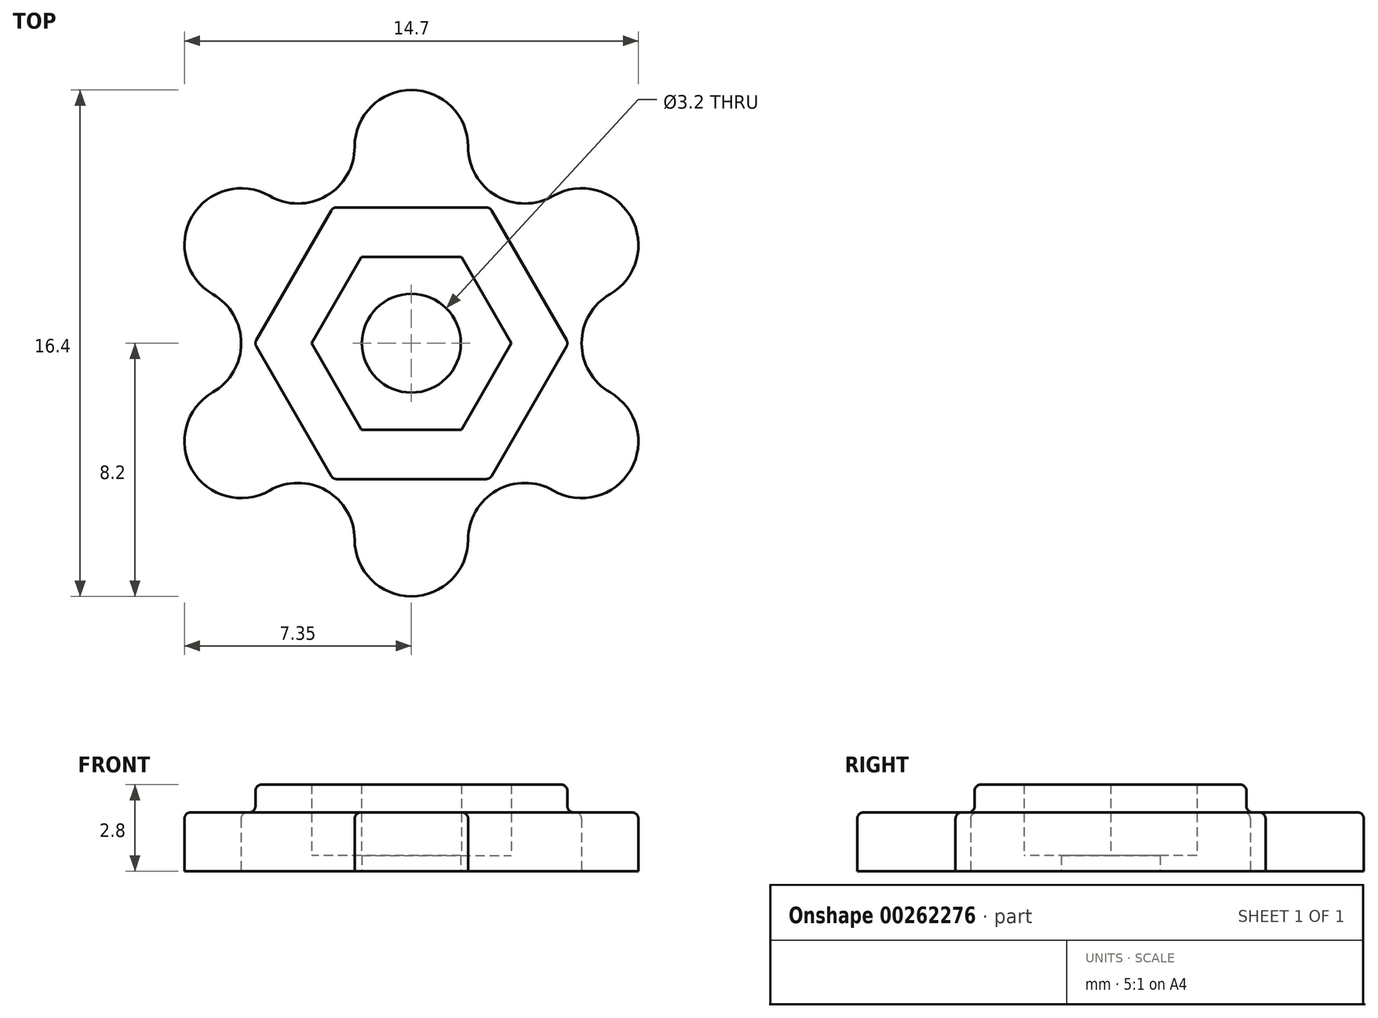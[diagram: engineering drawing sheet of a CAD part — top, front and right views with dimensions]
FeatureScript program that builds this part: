
annotation { "Feature Type Name" : "Feature", "Feature Type Description" : "" }
export const myFeature = defineFeature(function(context is Context, id is Id, definition is map)
    precondition{}
    {
        {
            var Q0;
            Q0=qCreatedBy(makeId("Top.planeOp"),FACE);
            var sketch = newSketch(context, id + "F0", { "sketchPlane" : qUnion([Q0])});
            skCircle(sketch, "E0", {"center": v(0, 0) * mm, "radius": 6.62 * mm, "construction": true});
            skArc(sketch, "E1", {"start": v(1.84, 6.36) * mm, "mid": v(0, 8.2) * mm, "end": v(-1.84, 6.36) * mm});
            skLineSegment(sketch, "E2", {"start": v(1.84, 6.36) * mm, "end": v(-1.84, 6.36) * mm, "construction": true});
            skArc(sketch, "E3", {"start": v(1.84, 6.36) * mm, "mid": v(2.76, 4.77) * mm, "end": v(4.6, 4.77) * mm});
            skLineSegment(sketch, "E4", {"start": v(1.84, 6.36) * mm, "end": v(4.6, 4.77) * mm, "construction": true});
            skArc(sketch, "E5.1.0", {"start": v(-4.6, 4.77) * mm, "mid": v(-7.1, 4.1) * mm, "end": v(-6.43, 1.6) * mm});
            skArc(sketch, "E5.1.1", {"start": v(-4.6, 4.77) * mm, "mid": v(-2.76, 4.77) * mm, "end": v(-1.84, 6.36) * mm});
            skArc(sketch, "E5.2.0", {"start": v(-6.43, -1.6) * mm, "mid": v(-7.1, -4.1) * mm, "end": v(-4.6, -4.77) * mm});
            skArc(sketch, "E5.2.1", {"start": v(-6.43, -1.6) * mm, "mid": v(-5.51, 0) * mm, "end": v(-6.43, 1.6) * mm});
            skArc(sketch, "E5.3.0", {"start": v(-1.84, -6.36) * mm, "mid": v(0, -8.2) * mm, "end": v(1.84, -6.36) * mm});
            skArc(sketch, "E5.3.1", {"start": v(-1.84, -6.36) * mm, "mid": v(-2.76, -4.77) * mm, "end": v(-4.6, -4.77) * mm});
            skArc(sketch, "E5.4.0", {"start": v(4.6, -4.77) * mm, "mid": v(7.1, -4.1) * mm, "end": v(6.43, -1.6) * mm});
            skArc(sketch, "E5.4.1", {"start": v(4.6, -4.77) * mm, "mid": v(2.76, -4.77) * mm, "end": v(1.84, -6.36) * mm});
            skArc(sketch, "E5.5.0", {"start": v(6.43, 1.6) * mm, "mid": v(7.1, 4.1) * mm, "end": v(4.6, 4.77) * mm});
            skArc(sketch, "E5.5.1", {"start": v(6.43, 1.6) * mm, "mid": v(5.51, 0) * mm, "end": v(6.43, -1.6) * mm});
            skCircle(sketch, "E6.cCircle", {"center": v(0, 0) * mm, "radius": 4.4 * mm, "construction": true});
            skLineSegment(sketch, "E6.0", {"start": v(2.54, 4.4) * mm, "end": v(5.08, 0) * mm});
            skLineSegment(sketch, "E6.1", {"start": v(5.08, 0) * mm, "end": v(2.54, -4.4) * mm});
            skLineSegment(sketch, "E6.2", {"start": v(2.54, -4.4) * mm, "end": v(-2.54, -4.4) * mm});
            skLineSegment(sketch, "E6.3", {"start": v(-2.54, -4.4) * mm, "end": v(-5.08, 0) * mm});
            skLineSegment(sketch, "E6.4", {"start": v(-5.08, 0) * mm, "end": v(-2.54, 4.4) * mm});
            skLineSegment(sketch, "E6.5", {"start": v(-2.54, 4.4) * mm, "end": v(2.54, 4.4) * mm});
            skPoint(sketch, "E6.0.midPoint", {"position": v(3.81, 2.2) * mm});
            skCircle(sketch, "E7.cCircle", {"center": v(0, 0) * mm, "radius": 2.8 * mm, "construction": true});
            skLineSegment(sketch, "E7.0", {"start": v(1.62, 2.8) * mm, "end": v(3.23, 0) * mm});
            skLineSegment(sketch, "E7.1", {"start": v(3.23, 0) * mm, "end": v(1.62, -2.8) * mm});
            skLineSegment(sketch, "E7.2", {"start": v(1.62, -2.8) * mm, "end": v(-1.62, -2.8) * mm});
            skLineSegment(sketch, "E7.3", {"start": v(-1.62, -2.8) * mm, "end": v(-3.23, 0) * mm});
            skLineSegment(sketch, "E7.4", {"start": v(-3.23, 0) * mm, "end": v(-1.62, 2.8) * mm});
            skLineSegment(sketch, "E7.5", {"start": v(-1.62, 2.8) * mm, "end": v(1.62, 2.8) * mm});
            skPoint(sketch, "E7.0.midPoint", {"position": v(2.42, 1.4) * mm});
            skCircle(sketch, "E8", {"center": v(0, 0) * mm, "radius": 1.6 * mm});
            skSolve(sketch);
        }
        {
            var Q0;
            Q0=makeQuery(id+"F0.imprint","IMPRINT",FACE,{"disambiguationData":[TD([[makeQuery(id+"F0.imprint","IMPRINT",EDGE,{"derivedFrom":sQuery(id+"F0.wireOp",EDGE,"E1")}),1.0]])]});
            extrude(context, id + "F1", {"entities" : qUnion([Q0]), "depth" : 1.9 * mm});
        }
        {
            var Q0;
            Q0=makeQuery(id+"F0.imprint","IMPRINT",FACE,{"disambiguationData":[TD([[makeQuery(id+"F0.imprint","IMPRINT",EDGE,{"derivedFrom":sQuery(id+"F0.wireOp",EDGE,"E6.0")}),-1.0]])]});
            extrude(context, id + "F2", {"entities" : qUnion([Q0]), "operationType" : NewBodyOperationType.ADD, "depth" : 2.8 * mm});
        }
        {
            var Q0;
            Q0=makeQuery(id+"F0.imprint","IMPRINT",FACE,{"disambiguationData":[TD([[makeQuery(id+"F0.imprint","IMPRINT",EDGE,{"derivedFrom":sQuery(id+"F0.wireOp",EDGE,"E7.0")}),-1.0]])]});
            extrude(context, id + "F3", {"entities" : qUnion([Q0]), "operationType" : NewBodyOperationType.ADD, "depth" : 0.5 * mm});
        }
        {
            var Q0;
            Q0=makeQuery(id+"F2.opExtrude","CAP_EDGE",EDGE,{"disambiguationData":[OSD([sQuery(id+"F0.wireOp",EDGE,"E6.1")])],"isStart":false});
            var Q1;
            Q1=makeQuery(id+"F2.opExtrude","SWEPT_EDGE",EDGE,{"disambiguationData":[OSD([sQuery(id+"F0.wireOp",EDGE,"E6.1"),sQuery(id+"F0.wireOp",EDGE,"E6.2")])]});
            var Q2;
            Q2=makeQuery(id+"F2.opExtrude","CAP_EDGE",EDGE,{"disambiguationData":[OSD([sQuery(id+"F0.wireOp",EDGE,"E6.2")])],"isStart":false});
            var Q3;
            Q3=makeQuery(id+"F2.opExtrude","SWEPT_EDGE",EDGE,{"disambiguationData":[OSD([sQuery(id+"F0.wireOp",EDGE,"E6.2"),sQuery(id+"F0.wireOp",EDGE,"E6.3")])]});
            var Q4;
            Q4=makeQuery(id+"F2.opExtrude","CAP_EDGE",EDGE,{"disambiguationData":[OSD([sQuery(id+"F0.wireOp",EDGE,"E6.3")])],"isStart":false});
            var Q5;
            Q5=makeQuery(id+"F2.opExtrude","CAP_EDGE",EDGE,{"disambiguationData":[OSD([sQuery(id+"F0.wireOp",EDGE,"E6.4")])],"isStart":false});
            var Q6;
            Q6=makeQuery(id+"F2.opExtrude","SWEPT_EDGE",EDGE,{"disambiguationData":[OSD([sQuery(id+"F0.wireOp",EDGE,"E6.3"),sQuery(id+"F0.wireOp",EDGE,"E6.4")])]});
            var Q7;
            Q7=makeQuery(id+"F2.opExtrude","SWEPT_EDGE",EDGE,{"disambiguationData":[OSD([sQuery(id+"F0.wireOp",EDGE,"E6.4"),sQuery(id+"F0.wireOp",EDGE,"E6.5")])]});
            var Q8;
            Q8=makeQuery(id+"F2.opExtrude","CAP_EDGE",EDGE,{"disambiguationData":[OSD([sQuery(id+"F0.wireOp",EDGE,"E6.5")])],"isStart":false});
            var Q9;
            Q9=makeQuery(id+"F2.opExtrude","SWEPT_EDGE",EDGE,{"disambiguationData":[OSD([sQuery(id+"F0.wireOp",EDGE,"E6.0"),sQuery(id+"F0.wireOp",EDGE,"E6.5")])]});
            var Q10;
            Q10=makeQuery(id+"F2.opExtrude","CAP_EDGE",EDGE,{"disambiguationData":[OSD([sQuery(id+"F0.wireOp",EDGE,"E6.0")])],"isStart":false});
            var Q11;
            Q11=makeQuery(id+"F2.opExtrude","SWEPT_EDGE",EDGE,{"disambiguationData":[OSD([sQuery(id+"F0.wireOp",EDGE,"E6.0"),sQuery(id+"F0.wireOp",EDGE,"E6.1")])]});
            fillet(context, id + "F4", {"entities" : qUnion([Q0, Q1, Q2, Q3, Q4, Q5, Q6, Q7, Q8, Q9, Q10, Q11]), "radius" : 0.2 * mm, "tangentPropagation" : true, "allowEdgeOverflow" : false});
        }
        {
            var Q0;
            Q0=makeQuery(id+"F1.opExtrude","CAP_FACE",FACE,{"disambiguationData":[OSD([sQuery(id+"F0.wireOp",EDGE,"E1"),sQuery(id+"F0.wireOp",EDGE,"E3"),sQuery(id+"F0.wireOp",EDGE,"E5.1.0"),sQuery(id+"F0.wireOp",EDGE,"E5.1.1"),sQuery(id+"F0.wireOp",EDGE,"E5.2.0"),sQuery(id+"F0.wireOp",EDGE,"E5.2.1"),sQuery(id+"F0.wireOp",EDGE,"E5.3.0"),sQuery(id+"F0.wireOp",EDGE,"E5.3.1"),sQuery(id+"F0.wireOp",EDGE,"E5.4.0"),sQuery(id+"F0.wireOp",EDGE,"E5.4.1"),sQuery(id+"F0.wireOp",EDGE,"E5.5.0"),sQuery(id+"F0.wireOp",EDGE,"E5.5.1"),sQuery(id+"F0.wireOp",EDGE,"E6.0"),sQuery(id+"F0.wireOp",EDGE,"E6.1"),sQuery(id+"F0.wireOp",EDGE,"E6.2"),sQuery(id+"F0.wireOp",EDGE,"E6.3"),sQuery(id+"F0.wireOp",EDGE,"E6.4"),sQuery(id+"F0.wireOp",EDGE,"E6.5")])],"isStart":false});
            fillet(context, id + "F5", {"entities" : qUnion([Q0]), "radius" : 0.2 * mm, "tangentPropagation" : true, "allowEdgeOverflow" : false});
        }
    });
